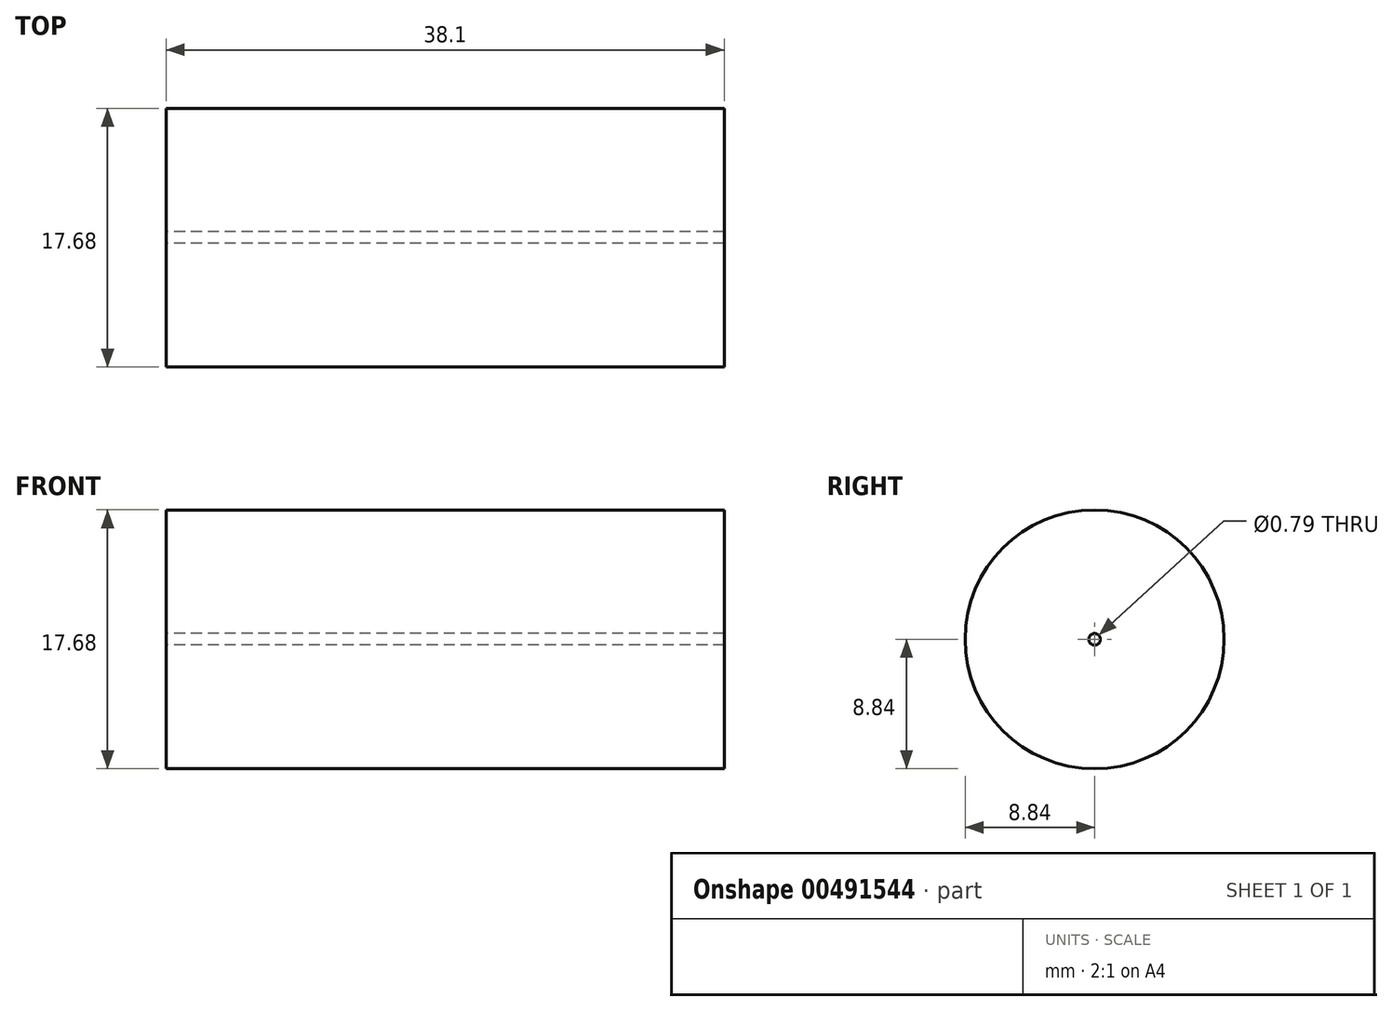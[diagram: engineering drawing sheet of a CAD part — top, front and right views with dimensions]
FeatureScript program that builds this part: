
annotation { "Feature Type Name" : "Feature", "Feature Type Description" : "" }
export const myFeature = defineFeature(function(context is Context, id is Id, definition is map)
    precondition{}
    {
        {
            var Q0;
            Q0=qCreatedBy(makeId("Right.planeOp"),FACE);
            var sketch = newSketch(context, id + "F0", { "sketchPlane" : qUnion([Q0])});
            skCircle(sketch, "E0", {"center": v(0, 0) * mm, "radius": 8.84 * mm});
            skCircle(sketch, "E1", {"center": v(0, 0) * mm, "radius": 0.4 * mm});
            skSolve(sketch);
        }
        {
            var Q0;
            Q0=makeQuery(id+"F0.imprint","IMPRINT",FACE,{"disambiguationData":[TD([[makeQuery(id+"F0.imprint","IMPRINT",EDGE,{"derivedFrom":sQuery(id+"F0.wireOp",EDGE,"E0")}),1.0]])]});
            extrude(context, id + "F1", {"entities" : qUnion([Q0]), "endBound" : BoundingType.SYMMETRIC, "depth" : 38.1 * mm});
        }
    });
